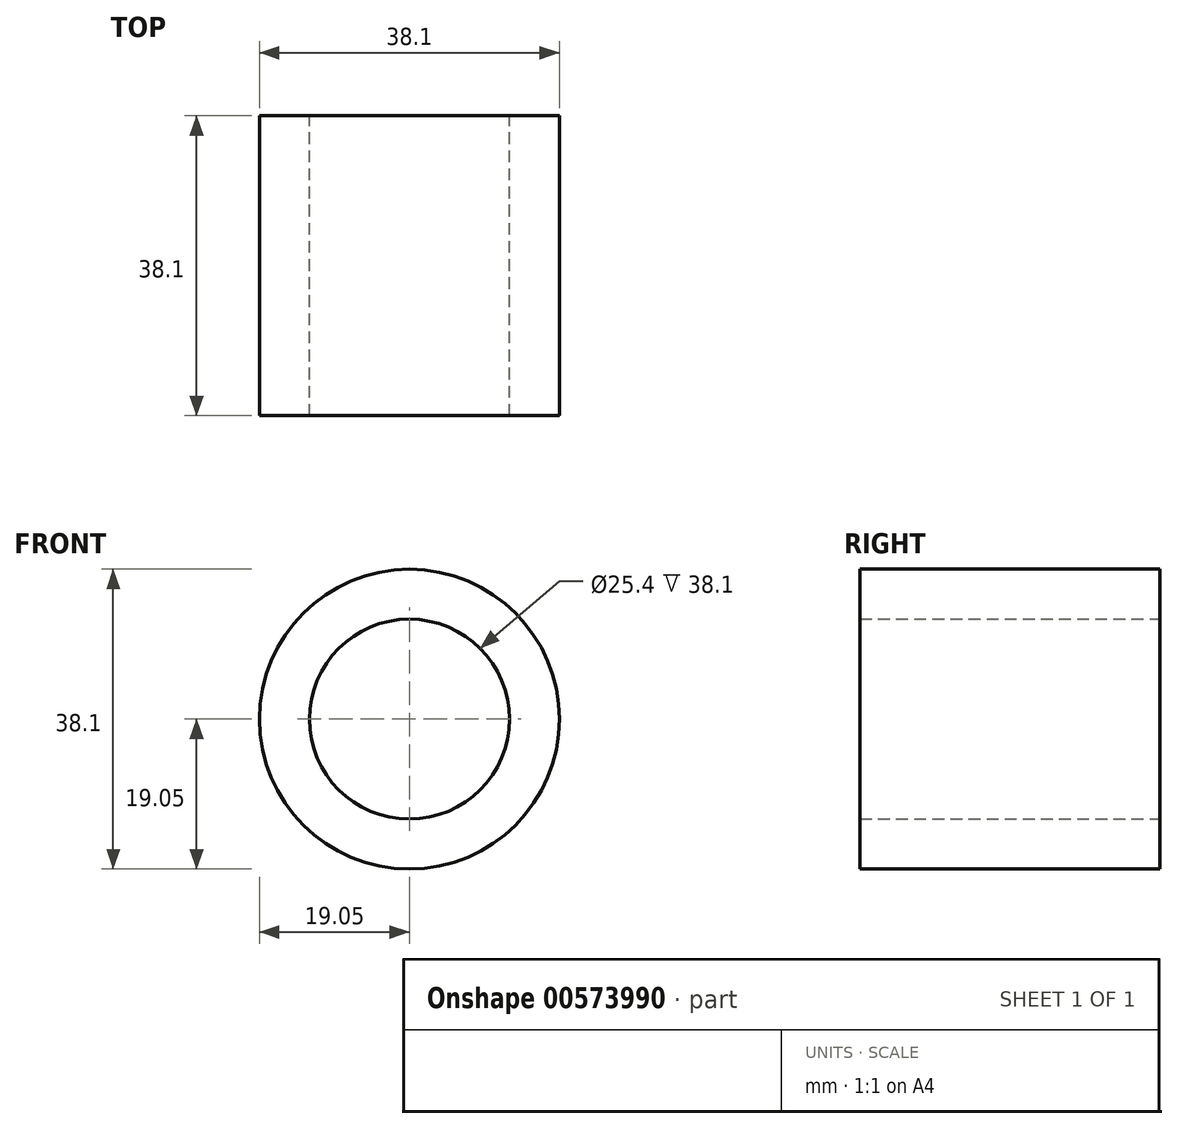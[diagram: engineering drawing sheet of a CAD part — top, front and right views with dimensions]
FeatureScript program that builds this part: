
annotation { "Feature Type Name" : "Feature", "Feature Type Description" : "" }
export const myFeature = defineFeature(function(context is Context, id is Id, definition is map)
    precondition{}
    {
        {
            var Q0;
            Q0=qCreatedBy(makeId("Front.planeOp"),FACE);
            var sketch = newSketch(context, id + "F0", { "sketchPlane" : qUnion([Q0])});
            skCircle(sketch, "E0", {"center": v(0, 0) * mm, "radius": 12.7 * mm});
            skCircle(sketch, "E1", {"center": v(0, 0) * mm, "radius": 19.05 * mm});
            skSolve(sketch);
        }
        {
            var Q0;
            Q0=makeQuery(id+"F0.imprint","IMPRINT",FACE,{"disambiguationData":[TD([[makeQuery(id+"F0.imprint","IMPRINT",EDGE,{"derivedFrom":sQuery(id+"F0.wireOp",EDGE,"E0")}),-1.0]])]});
            extrude(context, id + "F1", {"entities" : qUnion([Q0]), "depth" : 38.1 * mm, "offsetDistance" : 25.4 * mm});
        }
    });
